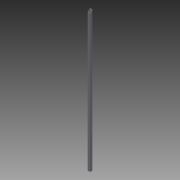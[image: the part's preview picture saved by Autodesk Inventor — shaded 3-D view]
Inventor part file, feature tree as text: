
AUTODESK INVENTOR PART (.ipt)
format: ipt  version: 2015 SP1 (Build 190203100, 203)  size: 105,472 bytes
history: native  units: mm
features: other x3, sketch x3
ambient origin geometry x8: Origin, YZ Plane, XZ Plane, XY Plane, X Axis, Y Axis, Z Axis, Center Point
bodies: Solid1 (feature_tree)
feature tree (6):
  other  "Poutre.ipt"
  other  "Solid1::Poutre.ipt"
  other  "TaggingFeature1"
  sketch  "Sketch1"  dims[d0=10.0mm]
  sketch  "Sketch2"
  sketch  "Sketch3"
